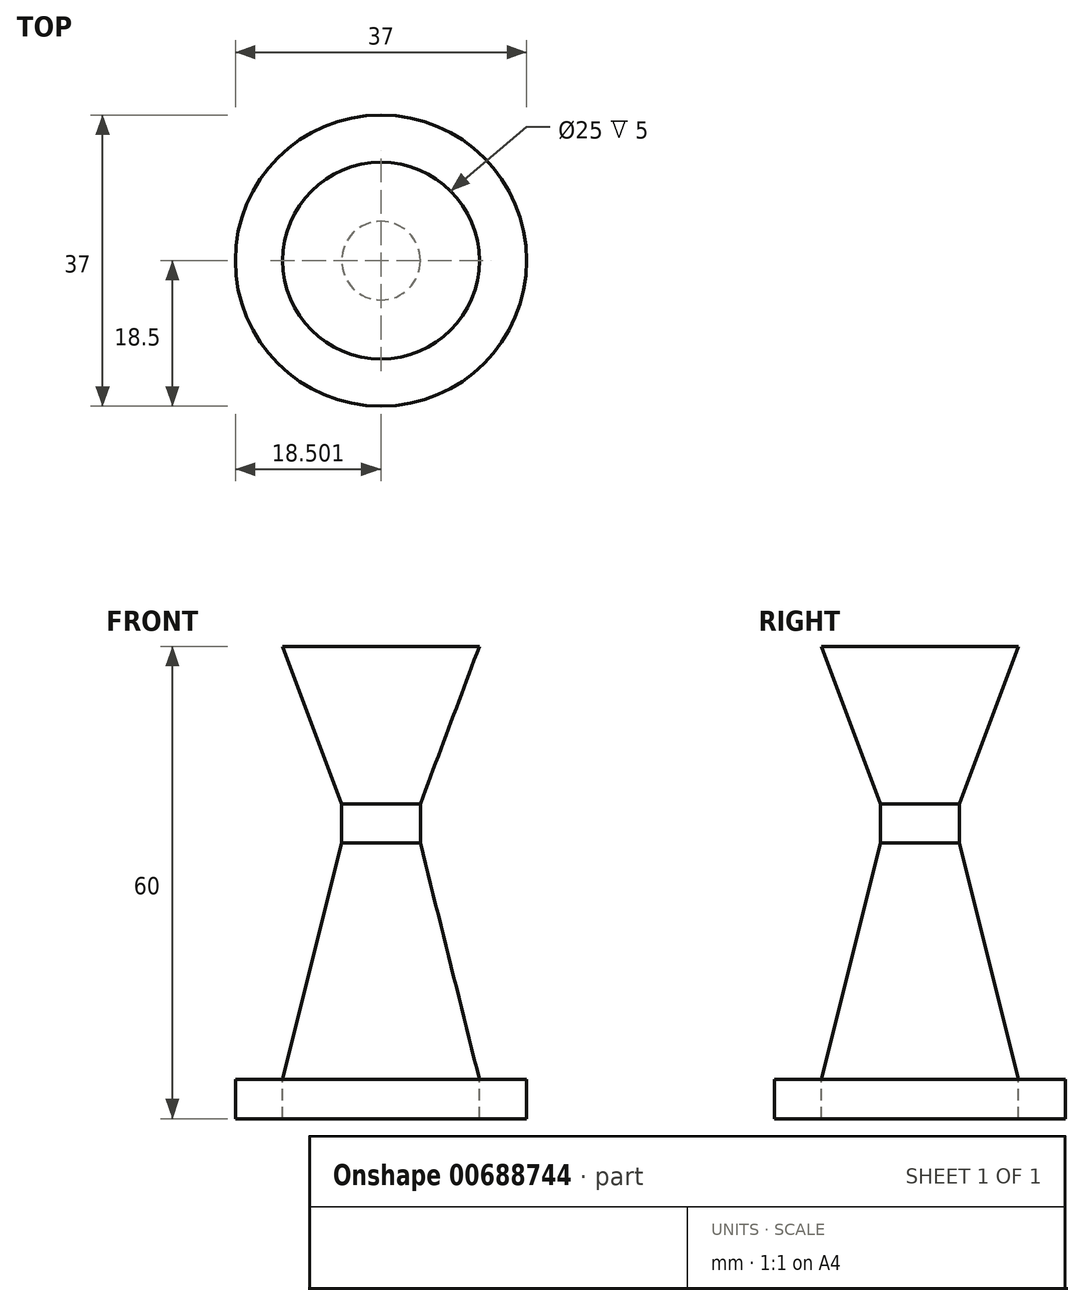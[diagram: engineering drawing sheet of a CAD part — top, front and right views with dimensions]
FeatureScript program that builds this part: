
annotation { "Feature Type Name" : "Feature", "Feature Type Description" : "" }
export const myFeature = defineFeature(function(context is Context, id is Id, definition is map)
    precondition{}
    {
        {
            var Q0;
            Q0=qCreatedBy(makeId("Front.planeOp"),FACE);
            var sketch = newSketch(context, id + "F0", { "sketchPlane" : qUnion([Q0])});
            skLineSegment(sketch, "E0", {"start": v(17.61, -20.2) * mm, "end": v(30.11, -20.2) * mm});
            skLineSegment(sketch, "E1", {"start": v(30.11, -20.2) * mm, "end": v(30.11, 9.8) * mm});
            skLineSegment(sketch, "E2", {"start": v(30.11, 9.8) * mm, "end": v(25.11, 9.8) * mm});
            skLineSegment(sketch, "E3", {"start": v(25.11, 9.8) * mm, "end": v(17.61, -20.2) * mm});
            skLineSegment(sketch, "E4", {"start": v(25.11, 9.8) * mm, "end": v(25.11, 14.8) * mm});
            skLineSegment(sketch, "E5", {"start": v(25.11, 14.8) * mm, "end": v(30.11, 14.8) * mm});
            skLineSegment(sketch, "E6", {"start": v(30.11, 14.8) * mm, "end": v(30.11, 13.56) * mm});
            skLineSegment(sketch, "E7", {"start": v(30.11, 14.8) * mm, "end": v(30.11, 34.8) * mm});
            skLineSegment(sketch, "E8", {"start": v(30.11, 34.8) * mm, "end": v(17.61, 34.8) * mm});
            skLineSegment(sketch, "E9", {"start": v(17.61, 34.8) * mm, "end": v(25.11, 14.8) * mm});
            skLineSegment(sketch, "E10.trimOffspring", {"start": v(30.11, 11.06) * mm, "end": v(30.11, 9.8) * mm});
            skPoint(sketch, "E11.center.orphan", {"position": v(30.11, 12.3) * mm});
            skLineSegment(sketch, "E12", {"start": v(30.11, 13.56) * mm, "end": v(25.11, 13.56) * mm});
            skLineSegment(sketch, "E13", {"start": v(25.11, 13.56) * mm, "end": v(25.11, 11.06) * mm});
            skLineSegment(sketch, "E14", {"start": v(30.11, 11.06) * mm, "end": v(25.11, 11.06) * mm});
            skLineSegment(sketch, "E15", {"start": v(30.11, 13.56) * mm, "end": v(30.11, 11.06) * mm});
            skSolve(sketch);
        }
        {
            var Q0;
            Q0=makeQuery(id+"F0.imprint","IMPRINT",FACE,{"disambiguationData":[TD([[makeQuery(id+"F0.imprint","IMPRINT",EDGE,{"derivedFrom":sQuery(id+"F0.wireOp",EDGE,"E0")}),1.0]])]});
            var Q1;
            Q1=makeQuery(id+"F0.imprint","IMPRINT",FACE,{"disambiguationData":[TD([[makeQuery(id+"F0.imprint","IMPRINT",EDGE,{"derivedFrom":sQuery(id+"F0.wireOp",EDGE,"E5")}),1.0]])]});
            var Q2;
            Q2=makeQuery(id+"F0.imprint","IMPRINT",FACE,{"disambiguationData":[TD([[makeQuery(id+"F0.imprint","IMPRINT",EDGE,{"derivedFrom":sQuery(id+"F0.wireOp",EDGE,"E2")}),-1.0]])]});
            var Q3;
            Q3=makeQuery(id+"F0.imprint","IMPRINT",FACE,{"disambiguationData":[TD([[makeQuery(id+"F0.imprint","IMPRINT",EDGE,{"derivedFrom":sQuery(id+"F0.wireOp",EDGE,"E12")}),1.0]])]});
            var Q4;
            {var subQ0=sQuery(id+"F0.wireOp",EDGE,"E5");Q4=makeQuery(id+"F0.imprint","IMPRINT",FACE,{"disambiguationData":[TD([[makeQuery(id+"F0.imprint","IMPRINT",EDGE,{"derivedFrom":subQ0}),-1.0]])]});}
            var Q5;
            Q5=sQuery(id+"F0.wireOp",EDGE,"E6");
            revolve(context, id + "F1", {"entities" : qUnion([Q0, Q1, Q2, Q3, Q4]), "axis" : qUnion([Q5]), "revolveType" : RevolveType.FULL});
        }
        {
            var Q0;
            Q0=makeQuery(id+"F1.opRevolve","SWEPT_FACE",FACE,{"disambiguationData":[OSD([sQuery(id+"F0.wireOp",EDGE,"E0")])]});
            var sketch = newSketch(context, id + "F2", { "sketchPlane" : qUnion([Q0])});
            skCircle(sketch, "E16", {"center": v(30.11, 0) * mm, "radius": 18.5 * mm});
            skSolve(sketch);
        }
        {
            var Q0;
            Q0=makeQuery(id+"F2.imprint","IMPRINT",FACE,{"disambiguationData":[TD([[makeQuery(id+"F2.imprint","IMPRINT",EDGE,{"derivedFrom":sQuery(id+"F2.wireOp",EDGE,"E16")}),1.0]])]});
            extrude(context, id + "F3", {"entities" : qUnion([Q0]), "depth" : 5 * mm, "offsetDistance" : 25 * mm});
        }
        {
            var Q0;
            Q0=makeQuery(id+"F1.opRevolve","SWEPT_FACE",FACE,{"disambiguationData":[OSD([sQuery(id+"F0.wireOp",EDGE,"E0")])]});
            extrude(context, id + "F4", {"entities" : qUnion([Q0]), "depth" : 5 * mm, "offsetDistance" : 25 * mm});
        }
    });
